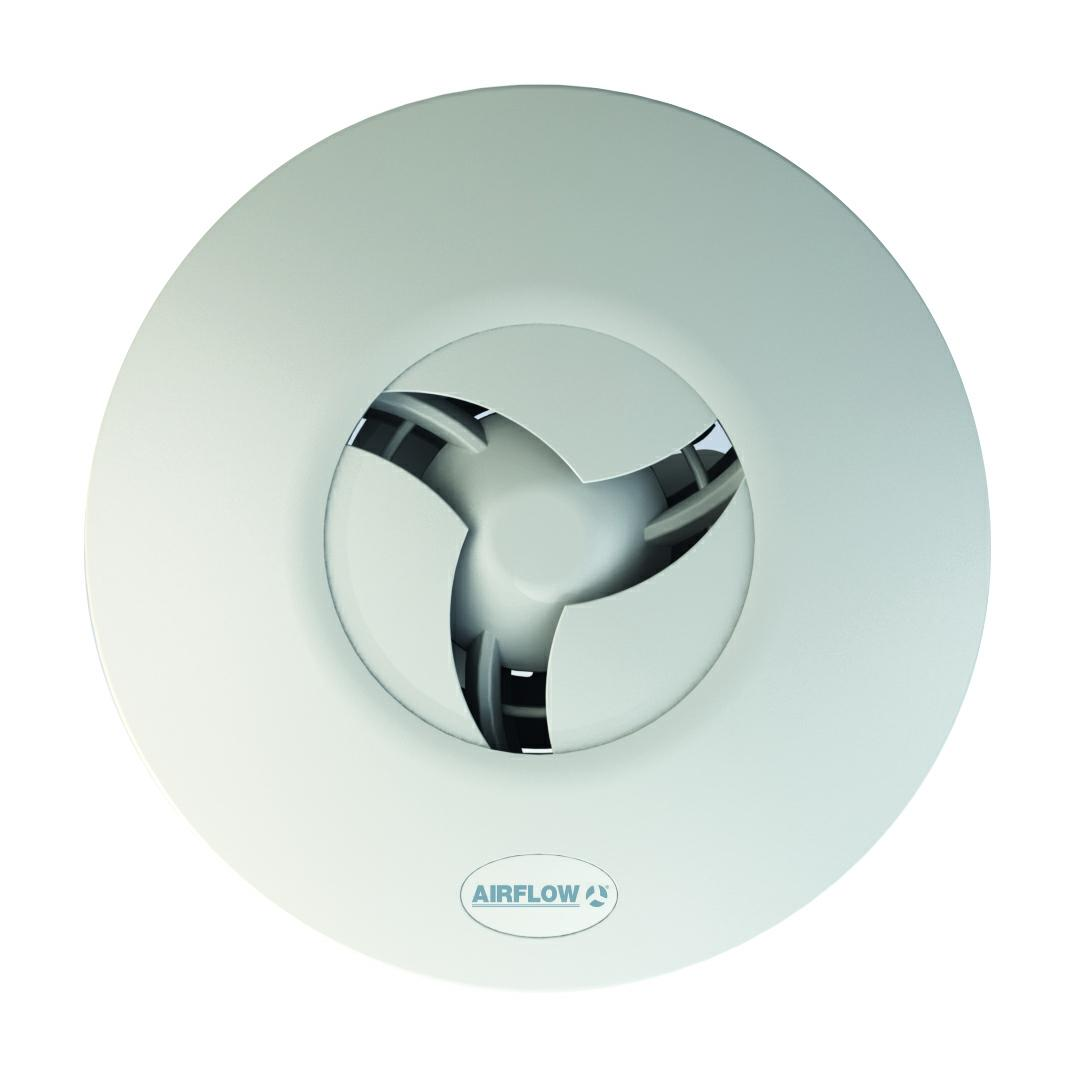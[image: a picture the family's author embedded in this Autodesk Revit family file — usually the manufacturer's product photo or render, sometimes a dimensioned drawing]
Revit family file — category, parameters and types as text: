
# Revit family: CADS_AIRFLOWdev_Fan_iCON30L_Smart
name_source: partatom
category: Mechanical Equipment
revit_build: Autodesk Revit 2016 (Build: 20150220_1215(x64)
units: mm (PartAtom-declared; Revit-internal decimal feet)

## family parameters
Cut with Voids When Loaded = No
Host = Face
Part Type = Normal
Room Calculation Point = No
Round Connector Dimension = Use Diameter
Shared = No

## types (1)
- iCONsmart 30L
    6MonthlyMaintenance = Visually inspect system, clean the fan and ducting if necessary
    A = 246 mm  [stored 0.807087 ft]
    AccessClearanceBottom = 350 mm
    AccessClearanceFront = 350 mm
    AccessClearanceLeft = 350 mm
    AccessClearanceRear = 0 mm  [stored 0 ft]
    AccessClearanceRight = 350 mm
    AccessClearanceTop = 350 mm
    AnthraciteFT = CADS_AIRFLOWdev_Fan_iCON30_Covers : Anthracite
    AssemblyPlace = UKNOWN
    AssetType = Fixed
    BMSLinks = No
    Body = CADS_AirFlow_White
    C = 67 mm
    CADS_Index = 0
    CEApproval = Yes
    CapacityControlType = Variable Speed Drive
    Category = Pr_65_67_29_05:Axial Flow Fans
    ChromeFT = CADS_AIRFLOWdev_Fan_iCON30_Covers : Chrome
    Color = White
    Controls = Basic on/off functionality controlled by external switch
The following additional, interchangeable modules can be fitted to the iCONsmart30:
Timer (72687224)
Humidity with Timer (72687225)
Motion sensor with timer  (72687226)
Motion sensor humidity timer (72687227)
    D = 125 mm  [stored 0.410105 ft]
    Default Elevation = 1219 mm
    Description = A smart intermittent extract fan with interchangeable modular controls and covers and a Red Dot Design Award winner and Quiet mark certified
    DesignOfDomesticVentilation = This fan should provide the minimum flow rates outlined and installed in line with Approved Document Part F of the Building Regulations.
    Ductwork = 125mm flexible or rigid
    DurationUnit = Year
    E = 56 mm  [stored 0.183727 ft]
    Exclusions = Hasn't been installed or used in accordance with the instructions
Connected with an unsuitable electrical supply
Has been misused, neglected or damaged
Modified or repaired by someone not authorised by Airflow Developments Ltd
Hasn't been installed according to Building Regulations or IEEE wiring regulations
    ExpectedServiceLife = 5
    ExternalExhaustAirTerminals = 90% free air grille
    Fan = Domestic intermittent axial fan
    Features = Smart intermittent
    Finish = Matte
    FireControlPanelLinks = No
    GlobalTradeItemNumber = 5019009325873
    Grade = Virgin
    GrossWeight = 1.00 kg
    HT = iCON_Smart_Modules : Humidity Timer
    HasPartWinding = Yes
    HasProtectiveEarth = No
    IP_Code = IPX5
    ISO140001 = Yes
    ISO90001 = Yes
    IfcExportAs = IfcFanType
    IfcExportType = NOTDEFINED
    InsulationStandardClass = Double Insulated
    IsExtendedWarranty = No
    IsGuarded = Yes
    MSHT = iCON_Smart_Modules : Motion Sensor Humidity Timer
    MST = iCON_Smart_Modules : Motion Sensor Timer
    Manufacturer = Airflow Developments Ltd
    ManufacturerAddress = Aidelle House
Lancaster Road
Cressex Business Park
High Wycombe
Bucks
HP123QP
    ManufacturerTelephone = 01494 525252
    ManufacturerWebsite = www.airflow.com
    Material = Plastic
    ModelLabel = iCONsmart 30L
    ModelReference = 72687222
    MotorDriveType = Direct Drive
    MotorEnclosureType = Totally Enclosed Air Over
    NBSCode = 90-45-30/310 Axial flow fans;
    NominalAirFlowRate = 42.0 L/s
    NominalFrequencyRange = 50-60
    NominalHeight = 246 mm  [stored 0.807087 ft]
    NominalLength = 123 mm  [stored 0.403543 ft]
    NominalPowerRate = 5 W
    NominalRotationSpeed = 45 Hz
    NominalStaticPressure = 35.0 Pa
    NominalWidth = 246 mm  [stored 0.807087 ft]
    NumberOfPoles = 1
    OperationAndMaintenanceManualAccessories = https://www.airflow.com
    OperationTemperatureRange = up to 40°C
    PointOfContact = Airflow Developments Ltd
    PowerSource = System-powered
    ProductLiteratureAccessories = https://www.airflow.com
    ProductionYear = 2017
    Quantity = 1
    QuietMarkApproval = Yes
    RatedCurrent = 3 A
    RatedVoltage = 21 V
    RedDotDesignAward = Yes
    ReplacementCost = 180
    RoomExtractAirTerminalDevices = En-suite, Utility and bathroom fan
    SandstoneFT = CADS_AIRFLOWdev_Fan_iCON30_Covers : Standstone
    ServiceLifeDuration = 5
    ServiceLifeType = ExpectedServiceLife
    Shape = Round
    ShippingWeight = 1.20 kg
    SilverFT = CADS_AIRFLOWdev_Fan_iCON30_Covers : Silver
    Size = 123 x 246 x 246
    StartingTime = 5.0 s
    Status = New
    SupplyPhase = 1
    TM = iCON_Smart_Modules : Timer
    Type = ICSM30
    Type Image = CADS_AIRFLOWdev_Fan_iCON30L_Smart.jpg
    Uniclass2015 = Pr_65_67_29_05
    WarrantyContent = Covered against faulty material or workmanship - not reinstallation if needed
    WarrantyGuarantor = Airflow Developments Ltd
    WarrantyPeriod = 5
    WarrantyPeriodForMotors = 1
    WarrantyPeriodWhenRegistered = 5

note: [stored X ft] marks values corroborated as IEEE doubles in the binary element streams (Revit-internal decimal feet)

## geometry (parser evidence)
native form markers: Blend x2, Sweep x7
no freeform markers — native parametric forms only
